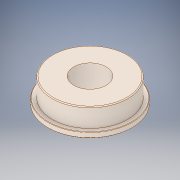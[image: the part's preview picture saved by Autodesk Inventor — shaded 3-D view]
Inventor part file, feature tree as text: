
AUTODESK INVENTOR PART (.ipt)
format: ipt  version: 2018 (Build 220112000, 112)  size: 146,432 bytes
history: native  units: in
note: dims shown in document units (in); Inventor stores cm internally (conversion verified against a paired STEP export)
features: fillet x1
ambient origin geometry x8: Origin, YZ Plane, XZ Plane, XY Plane, X Axis, Y Axis, Z Axis, Center Point
bodies: Solid1 (feature_tree)
feature tree (1):
  fillet  "Fillet2"  [1 undecoded]
note: 1 required parameter value undecoded (feature->parameter linkage not recoverable at this tier; creation-order binding heuristic only, values carry confidence <= 0.55)
